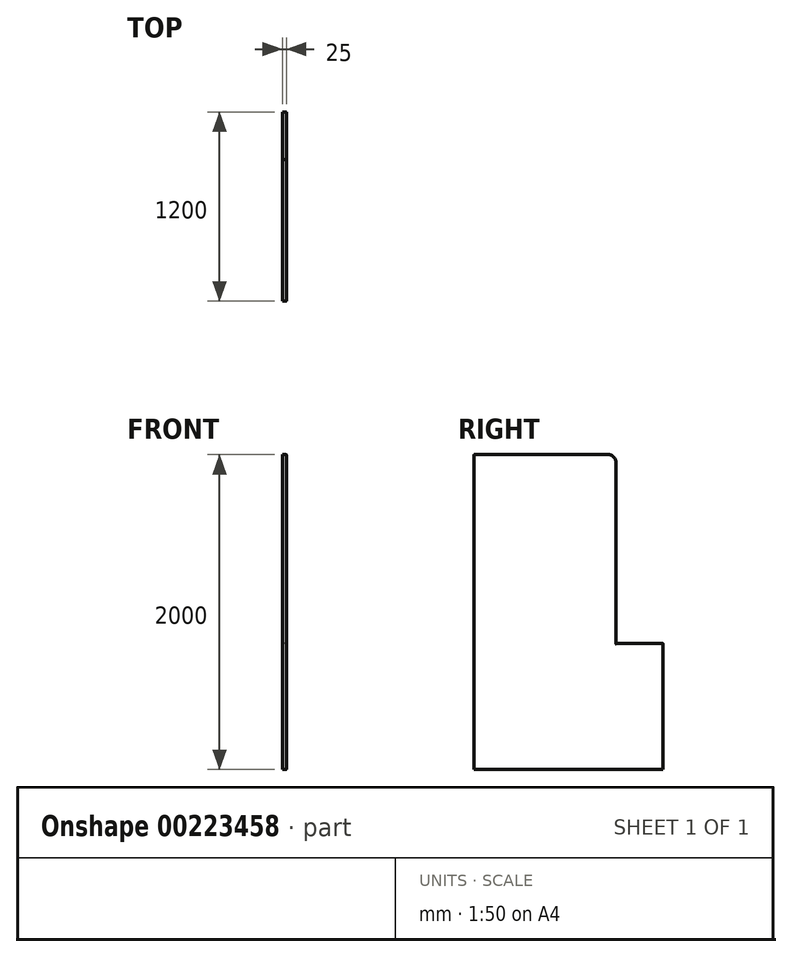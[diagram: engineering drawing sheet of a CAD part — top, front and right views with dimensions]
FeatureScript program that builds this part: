
annotation { "Feature Type Name" : "Feature", "Feature Type Description" : "" }
export const myFeature = defineFeature(function(context is Context, id is Id, definition is map)
    precondition{}
    {
        {
            var Q0;
            Q0=qCreatedBy(makeId("Right.planeOp"),FACE);
            var sketch = newSketch(context, id + "F0", { "sketchPlane" : qUnion([Q0])});
            skLineSegment(sketch, "E0", {"start": v(0, 0) * mm, "end": v(1200, 0) * mm});
            skLineSegment(sketch, "E1", {"start": v(1200, 0) * mm, "end": v(1200, 800) * mm});
            skLineSegment(sketch, "E2", {"start": v(1200, 800) * mm, "end": v(900, 800) * mm});
            skLineSegment(sketch, "E3", {"start": v(900, 800) * mm, "end": v(900, 2000) * mm});
            skLineSegment(sketch, "E4", {"start": v(900, 2000) * mm, "end": v(0, 2000) * mm});
            skLineSegment(sketch, "E5", {"start": v(0, 2000) * mm, "end": v(0, 0) * mm});
            skSolve(sketch);
        }
        {
            var Q0;
            Q0 = qSketchRegion(id + "F0", true);
            extrude(context, id + "F1", {"entities" : qUnion([Q0]), "depth" : 25 * mm});
        }
        {
            var Q0;
            Q0=makeQuery(id+"F1.opExtrude","CAP_FACE",FACE,{"disambiguationData":[OSD([sQuery(id+"F0.wireOp",EDGE,"E0"),sQuery(id+"F0.wireOp",EDGE,"E1"),sQuery(id+"F0.wireOp",EDGE,"E2"),sQuery(id+"F0.wireOp",EDGE,"E3"),sQuery(id+"F0.wireOp",EDGE,"E4"),sQuery(id+"F0.wireOp",EDGE,"E5")])],"isStart":false});
            fillet(context, id + "F2", {"entities" : qUnion([Q0]), "radius" : 3 * mm, "tangentPropagation" : true, "allowEdgeOverflow" : false});
        }
        {
            var Q0;
            Q0=makeQuery(id+"F1.opExtrude","SWEPT_EDGE",EDGE,{"disambiguationData":[OSD([sQuery(id+"F0.wireOp",EDGE,"E3"),sQuery(id+"F0.wireOp",EDGE,"E4")])]});
            fillet(context, id + "F3", {"entities" : qUnion([Q0]), "radius" : 50 * mm, "tangentPropagation" : true, "allowEdgeOverflow" : false});
        }
    });
